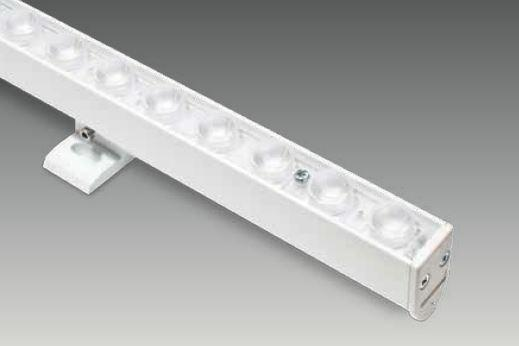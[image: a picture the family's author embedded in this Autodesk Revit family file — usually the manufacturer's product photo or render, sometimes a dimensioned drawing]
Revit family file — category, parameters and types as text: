
# Revit family: SD 0600 RUB
name_source: partatom
category: Lighting Fixtures
revit_build: Autodesk Revit 2017 (Build: 20160225_1515(x64)
units: mm (PartAtom-declared; Revit-internal decimal feet)

## family parameters
Cut with Voids When Loaded = No
Host = Face
Light Source = Yes
Part Type = Normal
Room Calculation Point = No
Round Connector Dimension = Use Diameter
Shared = No

## types (3) — shared parameters
Apparent Load = 23 VA
Color Filter = 16777215
Default Elevation = 1219 mm
Dimming Lamp Color Temperature Shift = <None>
Emit Shape Visible in Rendering = Yes
Emit from Rectangle Length = 20 mm  [stored 0.0656168 ft]
Emit from Rectangle Width = 600 mm
Light Source Symbol Size = 610 mm
Manufacturer = ARLIGHT
Type Image = SD 0600 RUB.JPG
Wattage Comments = 23W

## per-type parameters (varying)
| type | Beam Angle 1 | Beam Angle 2 |
| SDRUB.600.27.23.30 | 0.00° | 0.00° |
| SDRUB.600.38.23.30 | 0.00° | 0.00° |
| SDRUB.600.4520.23.30 | 20.00° | 45.00° |

note: [stored X ft] marks values corroborated as IEEE doubles in the binary element streams (Revit-internal decimal feet)

## geometry (parser evidence)
native form markers: Sweep x3
no freeform markers — native parametric forms only
